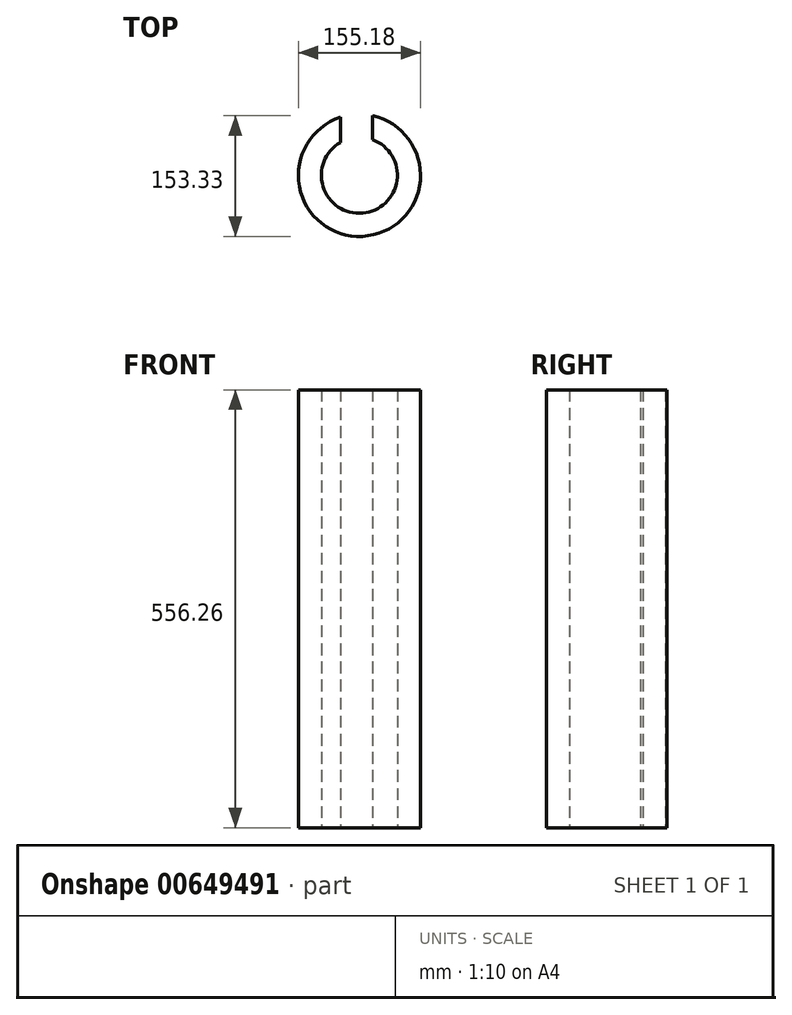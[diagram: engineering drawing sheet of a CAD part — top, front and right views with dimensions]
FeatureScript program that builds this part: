
annotation { "Feature Type Name" : "Feature", "Feature Type Description" : "" }
export const myFeature = defineFeature(function(context is Context, id is Id, definition is map)
    precondition{}
    {
        {
            var Q0;
            Q0=qCreatedBy(makeId("Top.planeOp"),FACE);
            var sketch = newSketch(context, id + "F0", { "sketchPlane" : qUnion([Q0])});
            skCircle(sketch, "E0", {"center": v(0, 0) * mm, "radius": 77.59 * mm});
            skCircle(sketch, "E1", {"center": v(0, 0) * mm, "radius": 48.27 * mm});
            skLineSegment(sketch, "E2", {"start": v(0, 0) * mm, "end": v(0, 77.59) * mm});
            skLineSegment(sketch, "E3", {"start": v(0, 77.59) * mm, "end": v(16.8, 77.59) * mm});
            skLineSegment(sketch, "E4", {"start": v(16.8, 77.59) * mm, "end": v(16.8, 0) * mm});
            skLineSegment(sketch, "E5", {"start": v(16.8, 0) * mm, "end": v(-24.17, 0) * mm});
            skLineSegment(sketch, "E6", {"start": v(-24.17, 0) * mm, "end": v(-24.17, 73.73) * mm});
            skSolve(sketch);
        }
        {
            var Q0;
            {var subQ0=sQuery(id+"F0.wireOp",EDGE,"E6");var subQ1=sQuery(id+"F0.wireOp",EDGE,"E0");var subQ2=makeQuery(id+"F0.imprint","INTERSECT",VERTEX,{"derivedFrom":[subQ1,subQ0]});Q0=makeQuery(id+"F0.imprint","IMPRINT",FACE,{"disambiguationData":[TD([[makeQuery(id+"F0.imprint","IMPRINT",EDGE,{"disambiguationData":[TD([[subQ2,-1.0]])],"derivedFrom":subQ1}),1.0]])]});}
            extrude(context, id + "F1", {"entities" : qUnion([Q0]), "depth" : 556.26 * mm, "offsetDistance" : 25.4 * mm});
        }
    });
